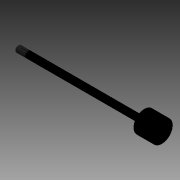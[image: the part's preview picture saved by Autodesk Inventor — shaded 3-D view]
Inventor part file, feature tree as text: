
AUTODESK INVENTOR PART (.ipt)
format: ipt  version: 2014 SP2 (Build 180246200, 246)  size: 149,504 bytes
history: native  units: in
note: dims shown in document units (in); Inventor stores cm internally (conversion verified against a paired STEP export)
features: other x98, sketch x3, revolve x2, thread x1, extrude x1
ambient origin geometry x8: Origin, YZ Plane, XZ Plane, XY Plane, X Axis, Y Axis, Z Axis, Center Point
bodies: Solid1 (feature_tree)
feature tree (105):
  revolve  "Revolution1"  Angle=360.0deg
  revolve  "Revolution2"  [1 undecoded]
  thread  "Thread1"  [1 undecoded]
  extrude  "Extrusion1"  [1 undecoded]
  other  "dia1_XY"
  other  "dia1_YZ"
  other  "dia1_ZX"
  other  "dia1_X"
  other  "dia1_Y"
  other  "dia1_Z"
  other  "dia1_Center"
  other  "dia12_XY"
  other  "dia12_YZ"
  other  "dia12_ZX"
  other  "dia12_X"
  other  "dia12_Y"
  other  "dia12_Z"
  other  "dia12_Center"
  other  "dia2_XY"
  other  "dia2_YZ"
  other  "dia2_ZX"
  other  "dia2_X"
  other  "dia2_Y"
  other  "dia2_Z"
  other  "dia2_Center"
  other  "dia22_XY"
  other  "dia22_YZ"
  other  "dia22_ZX"
  other  "dia22_X"
  other  "dia22_Y"
  other  "dia22_Z"
  other  "dia22_Center"
  other  "rl1_XY"
  other  "rl1_YZ"
  other  "rl1_ZX"
  other  "rl1_X"
  other  "rl1_Y"
  other  "rl1_Z"
  other  "rl1_Center"
  other  "rl2_XY"
  other  "rl2_YZ"
  other  "rl2_ZX"
  other  "rl2_X"
  other  "rl2_Y"
  other  "rl2_Z"
  other  "rl2_Center"
  other  "rod_cp_XY"
  other  "rod_cp_YZ"
  other  "rod_cp_ZX"
  other  "rod_cp_X"
  other  "rod_cp_Y"
  other  "rod_cp_Z"
  other  "rod_cp_Center"
  other  "thd1_XY"
  other  "thd1_YZ"
  other  "thd1_ZX"
  other  "thd1_X"
  other  "thd1_Y"
  other  "thd1_Z"
  other  "thd1_Center"
  other  "thd2_XY"
  other  "thd2_YZ"
  other  "thd2_ZX"
  other  "thd2_X"
  other  "thd2_Y"
  other  "thd2_Z"
  other  "thd2_Center"
  other  "to_rod_clevis_XY"
  other  "to_rod_clevis_YZ"
  other  "to_rod_clevis_ZX"
  other  "to_rod_clevis_X"
  other  "to_rod_clevis_Y"
  other  "to_rod_clevis_Z"
  other  "to_rod_clevis_Center"
  other  "wf1_XY"
  other  "wf1_YZ"
  other  "wf1_ZX"
  other  "wf1_X"
  other  "wf1_Y"
  other  "wf1_Z"
  other  "wf1_Center"
  other  "wf2_XY"
  other  "wf2_YZ"
  other  "wf2_ZX"
  other  "wf2_X"
  other  "wf2_Y"
  other  "wf2_Z"
  other  "wf2_Center"
  other  "wfw1_XY"
  other  "wfw1_YZ"
  other  "wfw1_ZX"
  other  "wfw1_X"
  other  "wfw1_Y"
  other  "wfw1_Z"
  other  "wfw1_Center"
  other  "wfw2_XY"
  other  "wfw2_YZ"
  other  "wfw2_ZX"
  other  "wfw2_X"
  other  "wfw2_Y"
  other  "wfw2_Z"
  other  "wfw2_Center"
  sketch  "Sketch_1"  dims[d0=360.0deg d1=360.0deg]
  sketch  "Sketch_3"  dims[d2=0.4752in d3=0.0in d4=0.125in d5=0.0in]
  sketch  "Sketch_10"  dims[d6=0.0in d7=0.0in d8=0.0in d9=0.0in d10=0.0in d11=0.0in d12=0.0in]
note: 3 required parameter values undecoded (feature->parameter linkage not recoverable at this tier; creation-order binding heuristic only, values carry confidence <= 0.55)